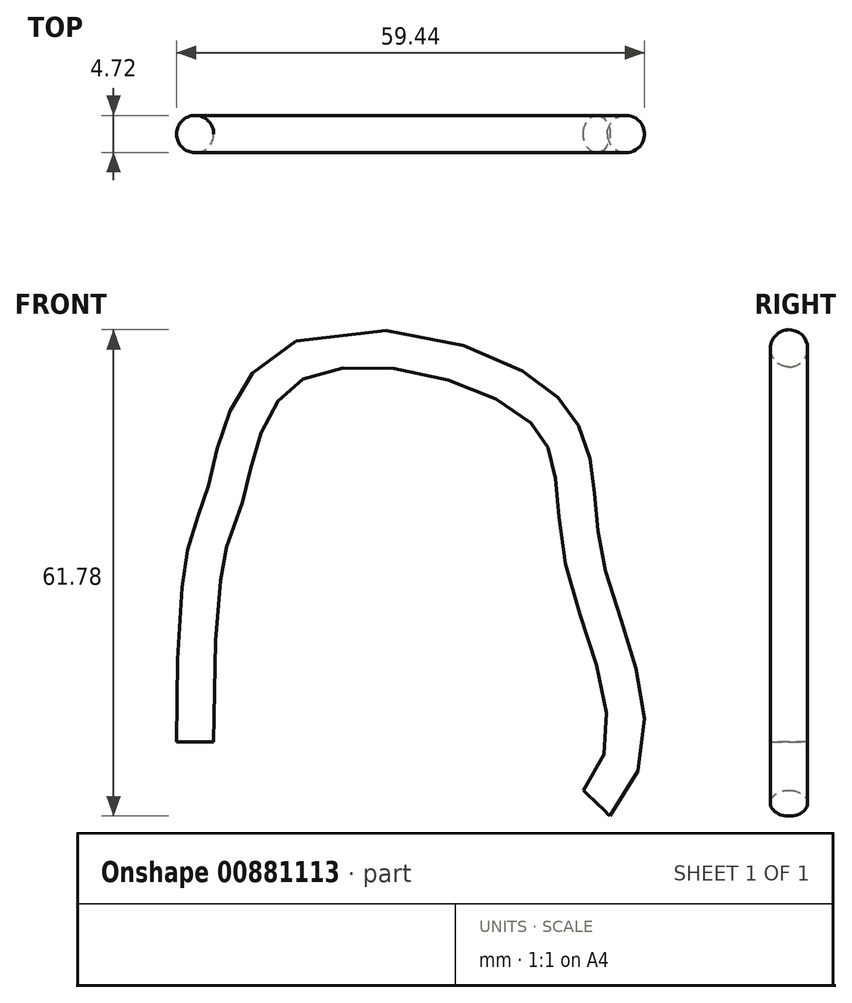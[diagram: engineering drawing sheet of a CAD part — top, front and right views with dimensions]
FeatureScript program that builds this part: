
annotation { "Feature Type Name" : "Feature", "Feature Type Description" : "" }
export const myFeature = defineFeature(function(context is Context, id is Id, definition is map)
    precondition{}
    {
        {
            var Q0;
            Q0=qCreatedBy(makeId("Front.planeOp"),FACE);
            var sketch = newSketch(context, id + "F0", { "sketchPlane" : qUnion([Q0])});
            skFitSpline(sketch, "E0", {"points": [v(0, 0) * mm, v(3.77, 31.27) * mm, v(12.2, 48) * mm, v(44.43, 42.11) * mm, v(49.38, 23.01) * mm, v(51.01, -7.76) * mm], "startDerivative": vector(0, 368.22) * mm, "endDerivative": vector(-113.68, -117.94) * mm});
            skSolve(sketch);
        }
        {
            var Q0;
            Q0=qCreatedBy(makeId("Top.planeOp"),FACE);
            var sketch = newSketch(context, id + "F1", { "sketchPlane" : qUnion([Q0])});
            skCircle(sketch, "E1", {"center": v(0, 0) * mm, "radius": 2.36 * mm});
            skSolve(sketch);
        }
        {
            var Q0;
            Q0=qSketchRegion(id+"F1",true);
            var Q1;
            Q1=qConstructionFilter(qBodyType(qCreatedBy(id+"F0",EDGE),BodyType.WIRE),ConstructionObject.NO);
            sweep(context, id + "F2", {"profiles" : qUnion([Q0]), "path" : qUnion([Q1])});
        }
    });
